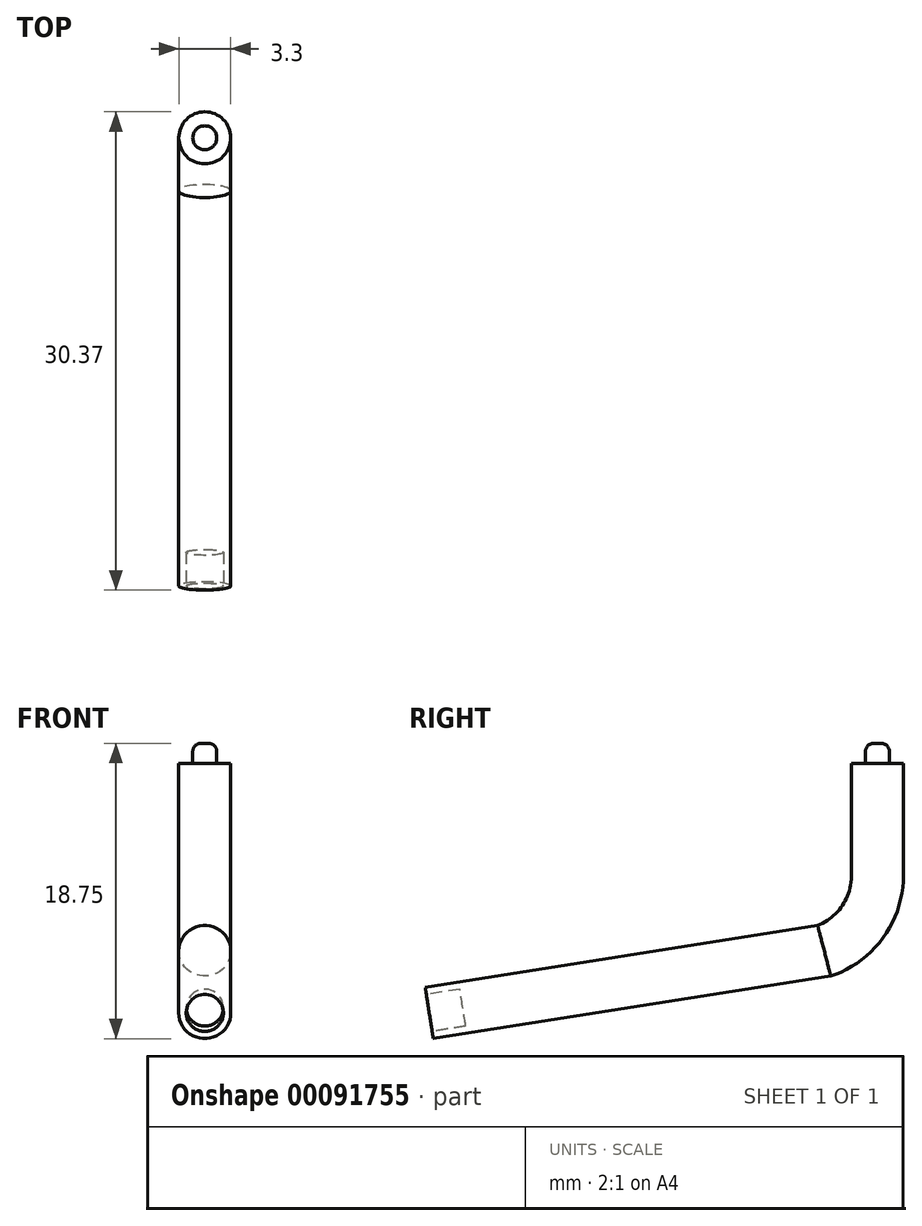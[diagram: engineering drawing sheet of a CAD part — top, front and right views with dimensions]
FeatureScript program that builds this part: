
annotation { "Feature Type Name" : "Feature", "Feature Type Description" : "" }
export const myFeature = defineFeature(function(context is Context, id is Id, definition is map)
    precondition{}
    {
        {
            var Q0;
            Q0=qCreatedBy(makeId("Right.planeOp"),FACE);
            var sketch = newSketch(context, id + "F0", { "sketchPlane" : qUnion([Q0])});
            skLineSegment(sketch, "E0", {"start": v(0, 0) * mm, "end": v(0, -7.11) * mm});
            skArc(sketch, "E1", {"start": v(-3.37, -11.9) * mm, "mid": v(-0.93, -10.04) * mm, "end": v(0, -7.11) * mm});
            skLineSegment(sketch, "E2", {"start": v(-3.37, -11.9) * mm, "end": v(-28.47, -15.84) * mm});
            skSolve(sketch);
        }
        {
            var Q0;
            Q0=qCreatedBy(makeId("Top.planeOp"),FACE);
            var sketch = newSketch(context, id + "F1", { "sketchPlane" : qUnion([Q0])});
            skCircle(sketch, "E3", {"center": v(0, 0) * mm, "radius": 1.65 * mm});
            skSolve(sketch);
        }
        {
            var Q0;
            Q0 = qSketchRegion(id + "F1", true);
            var Q1;
            Q1 = qConstructionFilter(qBodyType(qCreatedBy(id + "F0" ,EDGE), BodyType.WIRE), ConstructionObject.NO);
            sweep(context, id + "F2", {"profiles" : qUnion([Q0]), "path" : qUnion([Q1])});
        }
        {
            var Q0;
            Q0=makeQuery(id+"F2.opSweep","CAP_FACE",FACE,{"disambiguationData":[OSD([sQuery(id+"F0.wireOp",VERTEX,"E2.end"),sQuery(id+"F1.wireOp",EDGE,"E3")])],"isStart":false});
            var sketch = newSketch(context, id + "F3", { "sketchPlane" : qUnion([Q0])});
            skCircle(sketch, "E4", {"center": v(0, -11.23) * mm, "radius": 1.18 * mm});
            skSolve(sketch);
        }
        {
            var Q0;
            Q0 = qSketchRegion(id + "F3", true);
            extrude(context, id + "F4", {"entities" : qUnion([Q0]), "operationType" : NewBodyOperationType.REMOVE, "flatOperationType" : FlatOperationType.REMOVE, "oppositeDirection" : true, "offsetDistance" : 25.4 * mm, "depth" : 2.16 * mm, "domain" : OperationDomain.MODEL});
        }
        {
            var Q0;
            Q0=makeQuery(id+"F2.opSweep","CAP_FACE",FACE,{"disambiguationData":[OSD([sQuery(id+"F0.wireOp",VERTEX,"E0.start"),sQuery(id+"F1.wireOp",EDGE,"E3")])],"isStart":true});
            var sketch = newSketch(context, id + "F5", { "sketchPlane" : qUnion([Q0])});
            skCircle(sketch, "E5", {"center": v(0, 0) * mm, "radius": 0.76 * mm});
            skSolve(sketch);
        }
        {
            var Q0;
            Q0 = qSketchRegion(id + "F5", true);
            extrude(context, id + "F6", {"entities" : qUnion([Q0]), "operationType" : NewBodyOperationType.ADD, "depth" : 1.27 * mm});
        }
        {
            var Q0;
            Q0=makeQuery(id+"F6.opExtrude","CAP_EDGE",EDGE,{"disambiguationData":[OSD([sQuery(id+"F5.wireOp",EDGE,"E5")])],"isStart":false});
            fillet(context, id + "F7", {"entities" : qUnion([Q0]), "radius" : 0.5 * mm, "tangentPropagation" : true, "allowEdgeOverflow" : false});
        }
    });
